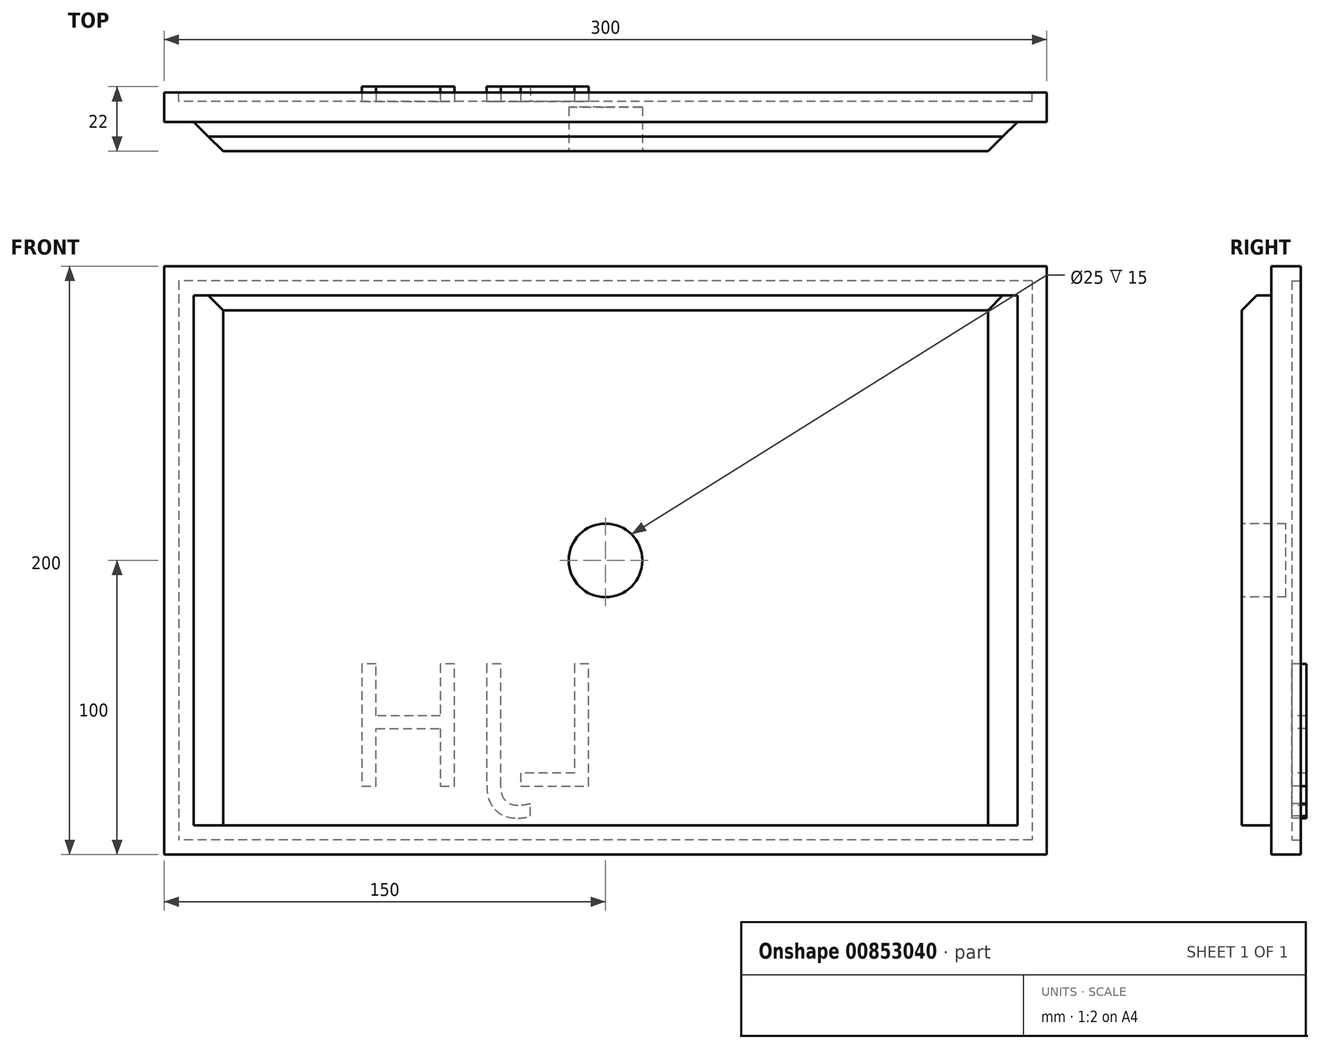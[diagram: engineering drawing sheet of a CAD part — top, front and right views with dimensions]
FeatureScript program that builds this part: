
annotation { "Feature Type Name" : "Feature", "Feature Type Description" : "" }
export const myFeature = defineFeature(function(context is Context, id is Id, definition is map)
    precondition{}
    {
        {
            var Q0;
            Q0=qCreatedBy(makeId("Front.planeOp"),FACE);
            var sketch = newSketch(context, id + "F0", { "sketchPlane" : qUnion([Q0])});
            skLineSegment(sketch, "E0.bottom", {"start": v(-150, 100) * mm, "end": v(150, 100) * mm});
            skLineSegment(sketch, "E0.top", {"start": v(-150, -100) * mm, "end": v(150, -100) * mm});
            skLineSegment(sketch, "E0.left", {"start": v(-150, 100) * mm, "end": v(-150, -100) * mm});
            skLineSegment(sketch, "E0.right", {"start": v(150, 100) * mm, "end": v(150, -100) * mm});
            skSolve(sketch);
        }
        {
            var Q0;
            Q0=makeQuery(id+"F0.imprint","IMPRINT",FACE,{"disambiguationData":[TD([[makeQuery(id+"F0.imprint","IMPRINT",EDGE,{"derivedFrom":sQuery(id+"F0.wireOp",EDGE,"E0.bottom")}),-1.0]])]});
            extrude(context, id + "F1", {"entities" : qUnion([Q0]), "depth" : 10 * mm, "offsetDistance" : 25 * mm});
        }
        {
            var Q0;
            Q0=makeQuery(id+"F1.opExtrude","CAP_FACE",FACE,{"disambiguationData":[OSD([sQuery(id+"F0.wireOp",EDGE,"E0.bottom"),sQuery(id+"F0.wireOp",EDGE,"E0.top"),sQuery(id+"F0.wireOp",EDGE,"E0.left"),sQuery(id+"F0.wireOp",EDGE,"E0.right")])],"isStart":false});
            var sketch = newSketch(context, id + "F2", { "sketchPlane" : qUnion([Q0])});
            skLineSegment(sketch, "E1.bottom", {"start": v(-140, 90) * mm, "end": v(140, 90) * mm});
            skLineSegment(sketch, "E1.top", {"start": v(-140, -90) * mm, "end": v(140, -90) * mm});
            skLineSegment(sketch, "E1.left", {"start": v(-140, 90) * mm, "end": v(-140, -90) * mm});
            skLineSegment(sketch, "E1.right", {"start": v(140, 90) * mm, "end": v(140, -90) * mm});
            skSolve(sketch);
        }
        {
            var Q0;
            Q0 = qSketchRegion(id + "F2", true);
            extrude(context, id + "F3", {"entities" : qUnion([Q0]), "operationType" : NewBodyOperationType.ADD, "depth" : 10 * mm, "offsetDistance" : 25 * mm});
        }
        {
            var Q0;
            Q0=makeQuery(id+"F3.opExtrude","CAP_EDGE",EDGE,{"disambiguationData":[OSD([sQuery(id+"F2.wireOp",EDGE,"E1.bottom")])],"isStart":false});
            var Q1;
            Q1=makeQuery(id+"F3.opExtrude","CAP_EDGE",EDGE,{"disambiguationData":[OSD([sQuery(id+"F2.wireOp",EDGE,"E1.top")])],"isStart":true});
            chamfer(context, id + "F4", {"entities" : qUnion([Q0, Q1]), "width" : 5 * mm, "tangentPropagation" : true});
        }
        {
            var Q0;
            Q0=makeQuery(id+"F3.opExtrude","CAP_EDGE",EDGE,{"disambiguationData":[OSD([sQuery(id+"F2.wireOp",EDGE,"E1.left")])],"isStart":false});
            var Q1;
            Q1=makeQuery(id+"F3.opExtrude","CAP_EDGE",EDGE,{"disambiguationData":[OSD([sQuery(id+"F2.wireOp",EDGE,"E1.right")])],"isStart":false});
            chamfer(context, id + "F5", {"entities" : qUnion([Q0, Q1]), "width" : 10 * mm, "tangentPropagation" : true});
        }
        {
            var Q0;
            Q0=makeQuery(id+"F3.opExtrude","CAP_FACE",FACE,{"disambiguationData":[OSD([sQuery(id+"F2.wireOp",EDGE,"E1.bottom"),sQuery(id+"F2.wireOp",EDGE,"E1.top"),sQuery(id+"F2.wireOp",EDGE,"E1.left"),sQuery(id+"F2.wireOp",EDGE,"E1.right")])],"isStart":false});
            var sketch = newSketch(context, id + "F6", { "sketchPlane" : qUnion([Q0])});
            skCircle(sketch, "E2", {"center": v(0, 0) * mm, "radius": 12.5 * mm});
            skSolve(sketch);
        }
        {
            var Q0;
            Q0 = qSketchRegion(id + "F6", true);
            extrude(context, id + "F7", {"entities" : qUnion([Q0]), "operationType" : NewBodyOperationType.REMOVE, "oppositeDirection" : true, "depth" : 15 * mm, "offsetDistance" : 25 * mm});
        }
        {
            var Q0;
            Q0=makeQuery(id+"F1.opExtrude","CAP_FACE",FACE,{"disambiguationData":[OSD([sQuery(id+"F0.wireOp",EDGE,"E0.bottom"),sQuery(id+"F0.wireOp",EDGE,"E0.top"),sQuery(id+"F0.wireOp",EDGE,"E0.left"),sQuery(id+"F0.wireOp",EDGE,"E0.right")])],"isStart":true});
            var sketch = newSketch(context, id + "F8", { "sketchPlane" : qUnion([Q0])});
            skLineSegment(sketch, "E3.bottom", {"start": v(-145, 95) * mm, "end": v(145, 95) * mm});
            skLineSegment(sketch, "E3.top", {"start": v(-145, -95) * mm, "end": v(145, -95) * mm});
            skLineSegment(sketch, "E3.left", {"start": v(-145, 95) * mm, "end": v(-145, -95) * mm});
            skLineSegment(sketch, "E3.right", {"start": v(145, 95) * mm, "end": v(145, -95) * mm});
            skSolve(sketch);
        }
        {
            var Q0;
            Q0 = qSketchRegion(id + "F8", true);
            extrude(context, id + "F9", {"entities" : qUnion([Q0]), "operationType" : NewBodyOperationType.REMOVE, "oppositeDirection" : true, "depth" : 3 * mm, "offsetDistance" : 25 * mm});
        }
        {
            var Q0;
            Q0=makeQuery(id+"F9.boolean.opBoolean","COPY",FACE,{"derivedFrom":makeQuery(id+"F9.opExtrude","CAP_FACE",FACE,{"disambiguationData":[OSD([sQuery(id+"F8.wireOp",EDGE,"E3.bottom"),sQuery(id+"F8.wireOp",EDGE,"E3.top"),sQuery(id+"F8.wireOp",EDGE,"E3.left"),sQuery(id+"F8.wireOp",EDGE,"E3.right")])],"isStart":false})});
            var sketch = newSketch(context, id + "F10", { "sketchPlane" : qUnion([Q0])});
            skText(sketch, "E4", { "text": "LJH", "fontName": "OpenSans-Regular.ttf"});
            const initialGuessF10  = {"E4": [0, -0.07669, 1, 0, 0.0418]};
            skSetInitialGuess(sketch, initialGuessF10);
            skSolve(sketch);
        }
        {
            var Q0;
            Q0 = qSketchRegion(id + "F10", true);
            extrude(context, id + "F11", {"entities" : qUnion([Q0]), "operationType" : NewBodyOperationType.ADD, "depth" : 5 * mm, "offsetDistance" : 25 * mm});
        }
    });
